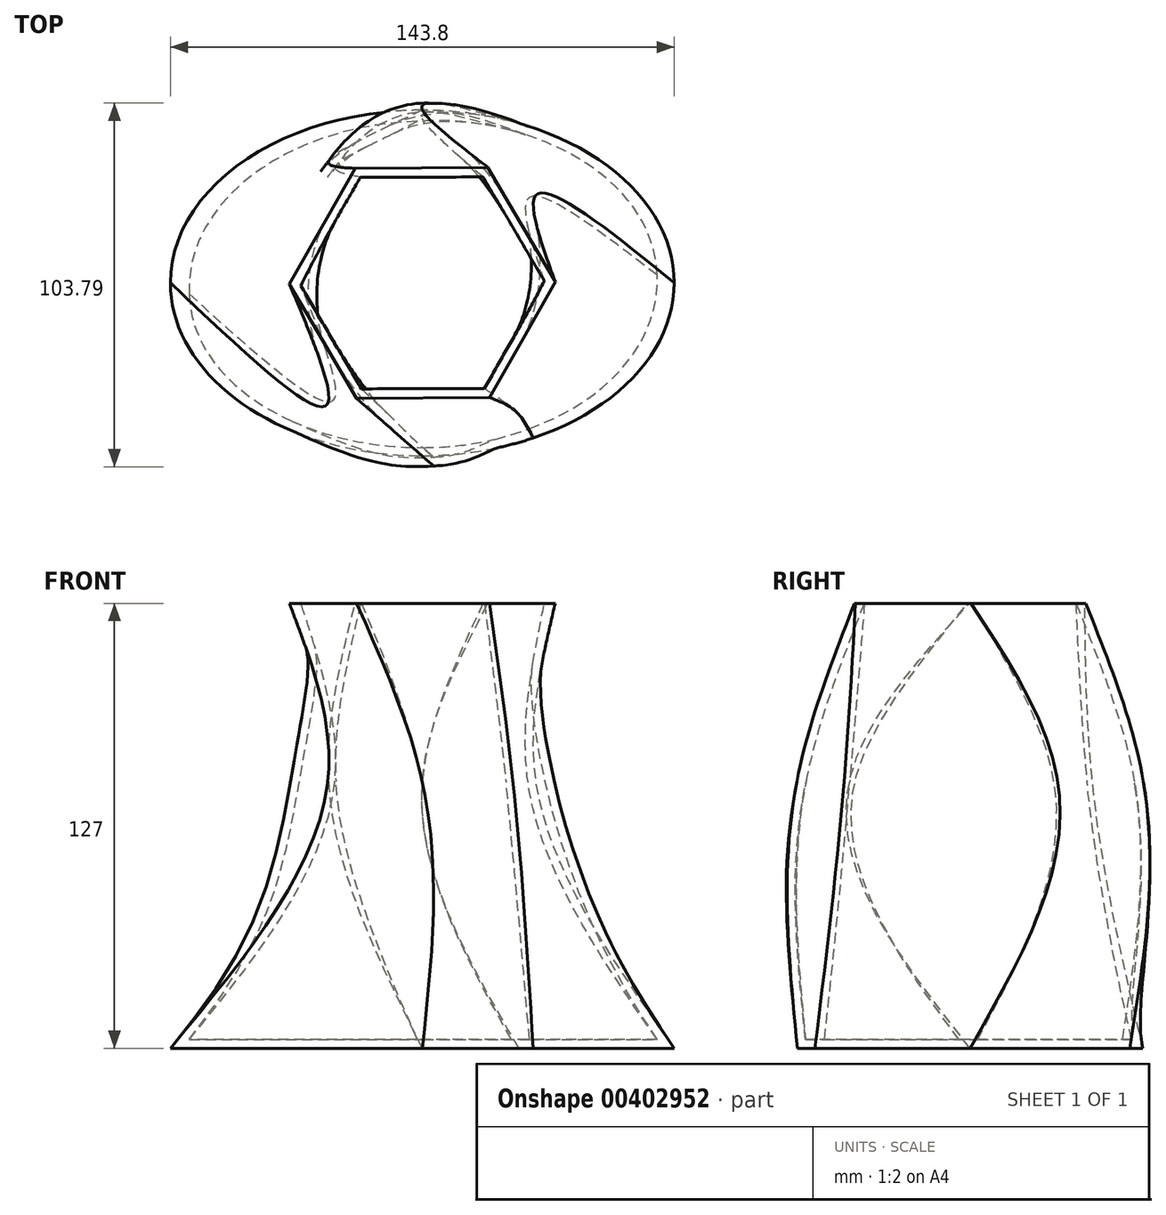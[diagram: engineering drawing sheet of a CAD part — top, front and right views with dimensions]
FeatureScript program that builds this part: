
annotation { "Feature Type Name" : "Feature", "Feature Type Description" : "" }
export const myFeature = defineFeature(function(context is Context, id is Id, definition is map)
    precondition{}
    {
        {
            var Q0;
            Q0=qCreatedBy(makeId("Top.planeOp"),FACE);
            var sketch = newSketch(context, id + "F0", { "sketchPlane" : qUnion([Q0])});
            skEllipticalArc(sketch, "E0", {});
            skEllipticalArc(sketch, "E1", {});
            skEllipticalArc(sketch, "E2", {});
            skEllipticalArc(sketch, "E3", {});
            skEllipticalArc(sketch, "E4", {});
            skEllipticalArc(sketch, "E5", {});
            const initialGuessF0  = {"E0": [0, 0, -1, 0, 0.07190267741680145, 0.04930181281130117, 0, 1.5707963267948966], "E1": [0, 0, -1, 0, 0.07190267741680145, 0.04930181281130117, 4.71238898038469, 0], "E2": [0, 0, -1, 0, 0.07190267741680145, 0.04930181281130117, 3.141592653589793, 4.3195620149931475], "E3": [0, 0, -1, 0, 0.07190267741680145, 0.04930181281130117, 1.5707963267948966, 2.0265099648914955], "E4": [0, 0, -1, 0, 0.07190267741680145, 0.04930181281130117, 2.0265099648914955, 3.141592653589793], "E5": [0, 0, -1, 0, 0.07190267741680145, 0.04930181281130117, 4.3195620149931475, 4.71238898038469]};
            skSetInitialGuess(sketch, initialGuessF0);
            skSolve(sketch);
        }
        {
            var Q0;
            Q0=qCreatedBy(makeId("Top.planeOp"),FACE);
            cPlane(context, id + "F1", {"entities" : qUnion([Q0]), "cplaneType" : CPlaneType.OFFSET, "offset" : 76.2 * mm, "width" : 152.4 * mm, "height" : 152.4 * mm});
        }
        {
            var Q0;
            Q0=qCreatedBy(id+"F1.planeOp",FACE);
            var sketch = newSketch(context, id + "F2", { "sketchPlane" : qUnion([Q0])});
            skEllipticalArc(sketch, "E6", {});
            skEllipticalArc(sketch, "E7", {});
            skEllipticalArc(sketch, "E8", {});
            skEllipticalArc(sketch, "E9", {});
            skEllipticalArc(sketch, "E10", {});
            skEllipticalArc(sketch, "E11", {});
            const initialGuessF2  = {"E6": [0, 0, 0, 1, 0.049441393464803696, 0.03763875837389604, 0, 0.7878508568873868], "E7": [0, 0, 0, 1, 0.049441393464803696, 0.03763875837389604, 3.141592653589793, 3.8982578990041516], "E8": [0, 0, 0, 1, 0.049441393464803696, 0.03763875837389604, 0.7878508568873868, 2.3418510809307183], "E9": [0, 0, 0, 1, 0.049441393464803696, 0.03763875837389604, 3.8982578990041516, 5.243776964347116], "E10": [0, 0, 0, 1, 0.049441393464803696, 0.03763875837389604, 5.243776964347116, 0], "E11": [0, 0, 0, 1, 0.049441393464803696, 0.03763875837389604, 2.3418510809307183, 3.141592653589793]};
            skSetInitialGuess(sketch, initialGuessF2);
            skSolve(sketch);
        }
        {
            var Q0;
            Q0=qCreatedBy(id+"F1.planeOp",FACE);
            cPlane(context, id + "F3", {"entities" : qUnion([Q0]), "cplaneType" : CPlaneType.OFFSET, "offset" : 50.8 * mm, "width" : 152.4 * mm, "height" : 152.4 * mm});
        }
        {
            var Q0;
            Q0=qCreatedBy(id+"F3.planeOp",FACE);
            var sketch = newSketch(context, id + "F4", { "sketchPlane" : qUnion([Q0])});
            skCircle(sketch, "E12.cCircle", {"center": v(0, 0) * mm, "radius": 32.85 * mm, "construction": true});
            skLineSegment(sketch, "E12.0", {"start": v(-37.94, -0.28) * mm, "end": v(-19.21, 32.71) * mm});
            skLineSegment(sketch, "E12.1", {"start": v(-19.21, 32.71) * mm, "end": v(18.72, 33) * mm});
            skLineSegment(sketch, "E12.2", {"start": v(18.72, 33) * mm, "end": v(37.94, 0.28) * mm});
            skLineSegment(sketch, "E12.3", {"start": v(37.94, 0.28) * mm, "end": v(19.21, -32.71) * mm});
            skLineSegment(sketch, "E12.4", {"start": v(19.21, -32.71) * mm, "end": v(-18.72, -33) * mm});
            skLineSegment(sketch, "E12.5", {"start": v(-18.72, -33) * mm, "end": v(-37.94, -0.28) * mm});
            skPoint(sketch, "E12.0.midPoint", {"position": v(-28.57, 16.21) * mm});
            skSolve(sketch);
        }
        {
            var Q0;
            Q0=makeQuery(id+"F0.imprint","IMPRINT",FACE,{"disambiguationData":[TD([[makeQuery(id+"F0.imprint","IMPRINT",EDGE,{"derivedFrom":sQuery(id+"F0.wireOp",EDGE,"E0")}),1.0]])]});
            var Q1;
            Q1=makeQuery(id+"F2.imprint","IMPRINT",FACE,{"disambiguationData":[TD([[makeQuery(id+"F2.imprint","IMPRINT",EDGE,{"derivedFrom":sQuery(id+"F2.wireOp",EDGE,"E6")}),1.0]])]});
            var Q2;
            Q2=makeQuery(id+"F4.imprint","IMPRINT",FACE,{"disambiguationData":[TD([[makeQuery(id+"F4.imprint","IMPRINT",EDGE,{"derivedFrom":sQuery(id+"F4.wireOp",EDGE,"E12.0")}),-1.0]])]});
            loft(context, id + "F5", {"sheetProfilesArray" : [{ "sheetProfileEntities" : qUnion([Q0]) }, { "sheetProfileEntities" : qUnion([Q1]) }, { "sheetProfileEntities" : qUnion([Q2]) }]});
        }
        {
            var Q0;
            Q0=makeQuery(id+"F5.opLoft","CAP_FACE",FACE,{"disambiguationData":[OSD([makeQuery(id+"F4.imprint","IMPRINT",FACE,{"disambiguationData":[TD([[makeQuery(id+"F4.imprint","IMPRINT",EDGE,{"derivedFrom":sQuery(id+"F4.wireOp",EDGE,"E12.0")}),-1.0]])]})])],"isStart":true});
            shell(context, id + "F6", {"entities" : qUnion([Q0]), "thickness" : 2.54 * mm});
        }
    });
